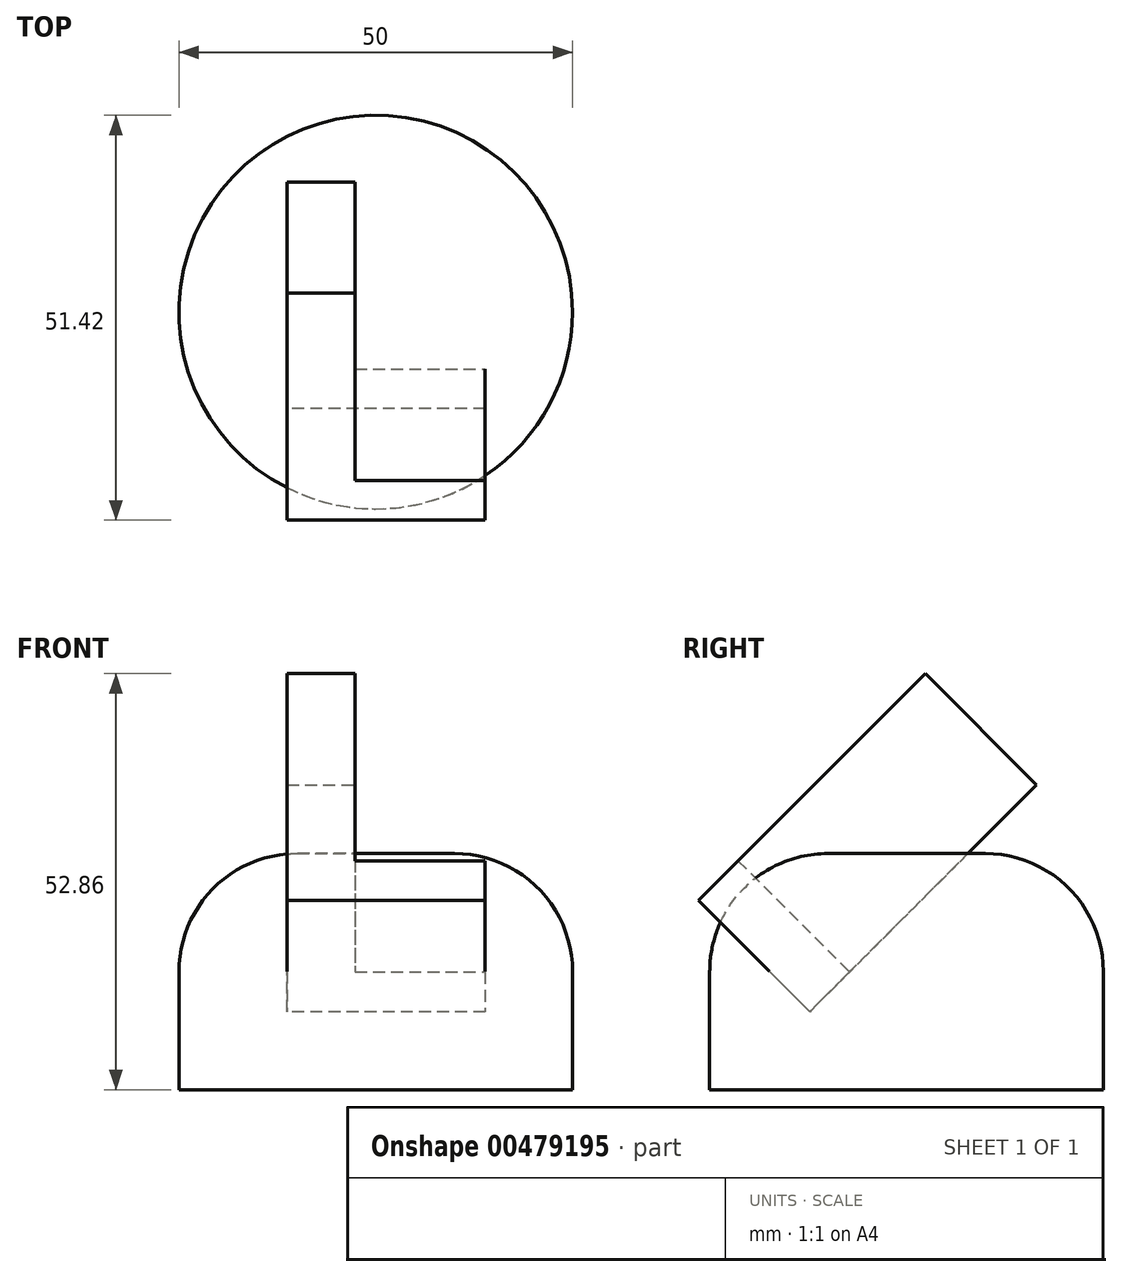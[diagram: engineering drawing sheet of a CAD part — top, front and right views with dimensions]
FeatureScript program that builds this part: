
annotation { "Feature Type Name" : "Feature", "Feature Type Description" : "" }
export const myFeature = defineFeature(function(context is Context, id is Id, definition is map)
    precondition{}
    {
        {
            var Q0;
            Q0=qCreatedBy(makeId("Top.planeOp"),FACE);
            var sketch = newSketch(context, id + "F0", { "sketchPlane" : qUnion([Q0])});
            skText(sketch, "E0", { "text": "L", "fontName": "OpenSans-Bold.ttf"});
            const initialGuessF0  = {"E0": [-0.09905, -0.02287, 1, 0, 0.0411]};
            skSetInitialGuess(sketch, initialGuessF0);
            skSolve(sketch);
        }
        {
            var Q0;
            Q0=qSketchRegion(id+"F0",true);
            extrude(context, id + "F1", {"entities" : qUnion([Q0]), "depth" : 20 * mm});
        }
        {
            var Q0;
            Q0=makeQuery(id+"F1.opExtrude","SWEPT_BODY",BODY,{"disambiguationData":[OSD([sQuery(id+"F0.wireOp",EDGE,"E0.sketch_text.stroke-0"),sQuery(id+"F0.wireOp",EDGE,"E0.sketch_text.stroke-1"),sQuery(id+"F0.wireOp",EDGE,"E0.sketch_text.stroke-2"),sQuery(id+"F0.wireOp",EDGE,"E0.sketch_text.stroke-3"),sQuery(id+"F0.wireOp",EDGE,"E0.sketch_text.stroke-4"),sQuery(id+"F0.wireOp",EDGE,"E0.sketch_text.stroke-5"),sQuery(id+"F0.wireOp",EDGE,"E0.sketch_text.stroke-6"),sQuery(id+"F0.wireOp",EDGE,"E0.sketch_text.stroke-7"),sQuery(id+"F0.wireOp",EDGE,"E0.sketch_text.stroke-8"),sQuery(id+"F0.wireOp",EDGE,"E0.sketch_text.stroke-9"),sQuery(id+"F0.wireOp",EDGE,"E0.sketch_text.stroke-10"),sQuery(id+"F0.wireOp",EDGE,"E0.sketch_text.stroke-11"),sQuery(id+"F0.wireOp",EDGE,"E0.sketch_text.stroke-12"),sQuery(id+"F0.wireOp",EDGE,"E0.sketch_text.stroke-13")])]});
            transform(context, id + "F2", {"entities" : qUnion([Q0]), "transformType" : TransformType.TRANSLATION_3D, "dx" : 76.45 * mm, "dy" : 0 * mm, "dz" : 0 * mm, "makeCopy" : false});
        }
        {
            var Q0;
            Q0=qCreatedBy(makeId("Top.planeOp"),FACE);
            var sketch = newSketch(context, id + "F3", { "sketchPlane" : qUnion([Q0])});
            skCircle(sketch, "E1", {"center": v(-27.2, 27.91) * mm, "radius": 25 * mm});
            skSolve(sketch);
        }
        {
            var Q0;
            Q0=makeQuery(id+"F1.opExtrude","SWEPT_BODY",BODY,{"disambiguationData":[OSD([sQuery(id+"F0.wireOp",EDGE,"E0.sketch_text.stroke-0"),sQuery(id+"F0.wireOp",EDGE,"E0.sketch_text.stroke-1"),sQuery(id+"F0.wireOp",EDGE,"E0.sketch_text.stroke-2"),sQuery(id+"F0.wireOp",EDGE,"E0.sketch_text.stroke-3"),sQuery(id+"F0.wireOp",EDGE,"E0.sketch_text.stroke-4"),sQuery(id+"F0.wireOp",EDGE,"E0.sketch_text.stroke-5"),sQuery(id+"F0.wireOp",EDGE,"E0.sketch_text.stroke-6"),sQuery(id+"F0.wireOp",EDGE,"E0.sketch_text.stroke-7"),sQuery(id+"F0.wireOp",EDGE,"E0.sketch_text.stroke-8"),sQuery(id+"F0.wireOp",EDGE,"E0.sketch_text.stroke-9"),sQuery(id+"F0.wireOp",EDGE,"E0.sketch_text.stroke-10"),sQuery(id+"F0.wireOp",EDGE,"E0.sketch_text.stroke-11"),sQuery(id+"F0.wireOp",EDGE,"E0.sketch_text.stroke-12"),sQuery(id+"F0.wireOp",EDGE,"E0.sketch_text.stroke-13")])]});
            transform(context, id + "F4", {"entities" : qUnion([Q0]), "transformType" : TransformType.TRANSLATION_3D, "dx" : 27.3 * mm, "dy" : 0 * mm, "dz" : 0 * mm, "makeCopy" : false});
        }
        {
            var Q0;
            Q0=makeQuery(id+"F3.imprint","IMPRINT",FACE,{"disambiguationData":[TD([[makeQuery(id+"F3.imprint","IMPRINT",EDGE,{"derivedFrom":sQuery(id+"F3.wireOp",EDGE,"E1")}),1.0]])]});
            extrude(context, id + "F5", {"entities" : qUnion([Q0]), "depth" : 30 * mm});
        }
        {
            var Q0;
            Q0=makeQuery(id+"F5.opExtrude","CAP_FACE",FACE,{"disambiguationData":[OSD([sQuery(id+"F3.wireOp",EDGE,"E1")])],"isStart":false});
            fillet(context, id + "F6", {"entities" : qUnion([Q0]), "radius" : 15 * mm, "tangentPropagation" : true, "allowEdgeOverflow" : false});
        }
        {
            var Q0;
            Q0=makeQuery(id+"F1.opExtrude","SWEPT_BODY",BODY,{"disambiguationData":[OSD([sQuery(id+"F0.wireOp",EDGE,"E0.sketch_text.stroke-0"),sQuery(id+"F0.wireOp",EDGE,"E0.sketch_text.stroke-1"),sQuery(id+"F0.wireOp",EDGE,"E0.sketch_text.stroke-2"),sQuery(id+"F0.wireOp",EDGE,"E0.sketch_text.stroke-3"),sQuery(id+"F0.wireOp",EDGE,"E0.sketch_text.stroke-4"),sQuery(id+"F0.wireOp",EDGE,"E0.sketch_text.stroke-5"),sQuery(id+"F0.wireOp",EDGE,"E0.sketch_text.stroke-6"),sQuery(id+"F0.wireOp",EDGE,"E0.sketch_text.stroke-7"),sQuery(id+"F0.wireOp",EDGE,"E0.sketch_text.stroke-8"),sQuery(id+"F0.wireOp",EDGE,"E0.sketch_text.stroke-9"),sQuery(id+"F0.wireOp",EDGE,"E0.sketch_text.stroke-10"),sQuery(id+"F0.wireOp",EDGE,"E0.sketch_text.stroke-11"),sQuery(id+"F0.wireOp",EDGE,"E0.sketch_text.stroke-12"),sQuery(id+"F0.wireOp",EDGE,"E0.sketch_text.stroke-13")])]});
            var Q1;
            Q1=makeQuery(id+"F1.opExtrude","CAP_EDGE",EDGE,{"disambiguationData":[OSD([sQuery(id+"F0.wireOp",EDGE,"E0.sketch_text.stroke-5")])],"isStart":true});
            transform(context, id + "F7", {"entities" : qUnion([Q0]), "transformType" : TransformType.ROTATION, "transformAxis" : qUnion([Q1]), "angle" : 45 * degree, "oppositeDirection" : true, "makeCopy" : false});
        }
        {
            var Q0;
            Q0=makeQuery(id+"F1.opExtrude","SWEPT_BODY",BODY,{"disambiguationData":[OSD([sQuery(id+"F0.wireOp",EDGE,"E0.sketch_text.stroke-0"),sQuery(id+"F0.wireOp",EDGE,"E0.sketch_text.stroke-1"),sQuery(id+"F0.wireOp",EDGE,"E0.sketch_text.stroke-2"),sQuery(id+"F0.wireOp",EDGE,"E0.sketch_text.stroke-3"),sQuery(id+"F0.wireOp",EDGE,"E0.sketch_text.stroke-4"),sQuery(id+"F0.wireOp",EDGE,"E0.sketch_text.stroke-5"),sQuery(id+"F0.wireOp",EDGE,"E0.sketch_text.stroke-6"),sQuery(id+"F0.wireOp",EDGE,"E0.sketch_text.stroke-7"),sQuery(id+"F0.wireOp",EDGE,"E0.sketch_text.stroke-8"),sQuery(id+"F0.wireOp",EDGE,"E0.sketch_text.stroke-9"),sQuery(id+"F0.wireOp",EDGE,"E0.sketch_text.stroke-10"),sQuery(id+"F0.wireOp",EDGE,"E0.sketch_text.stroke-11"),sQuery(id+"F0.wireOp",EDGE,"E0.sketch_text.stroke-12"),sQuery(id+"F0.wireOp",EDGE,"E0.sketch_text.stroke-13")])]});
            transform(context, id + "F8", {"entities" : qUnion([Q0]), "transformType" : TransformType.TRANSLATION_3D, "dx" : -48.3 * mm, "dy" : 38.5 * mm, "dz" : 9.9 * mm, "makeCopy" : false});
        }
    });
